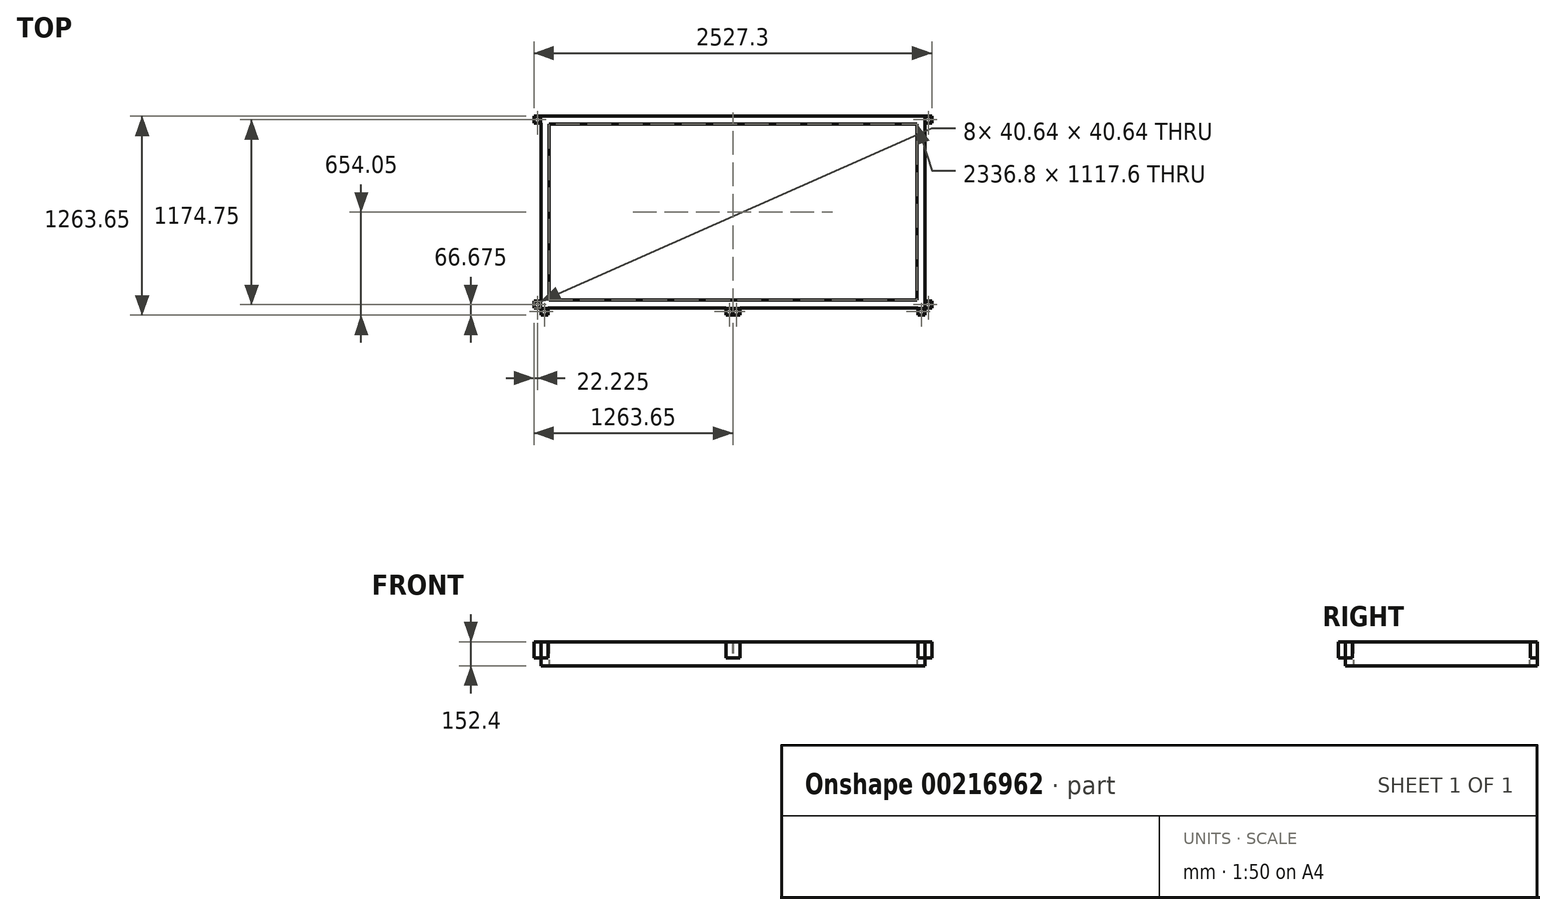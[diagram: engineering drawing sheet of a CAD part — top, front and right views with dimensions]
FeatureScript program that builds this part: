
annotation { "Feature Type Name" : "Feature", "Feature Type Description" : "" }
export const myFeature = defineFeature(function(context is Context, id is Id, definition is map)
    precondition{}
    {
        {
            var Q0;
            Q0=qCreatedBy(makeId("Top.planeOp"),FACE);
            var sketch = newSketch(context, id + "F0", { "sketchPlane" : qUnion([Q0])});
            skLineSegment(sketch, "E0.bottom", {"start": v(1219.2, 609.6) * mm, "end": v(-1219.2, 609.6) * mm});
            skLineSegment(sketch, "E0.top", {"start": v(1219.2, -609.6) * mm, "end": v(-1219.2, -609.6) * mm});
            skLineSegment(sketch, "E0.left", {"start": v(1219.2, 609.6) * mm, "end": v(1219.2, -609.6) * mm});
            skLineSegment(sketch, "E0.right", {"start": v(-1219.2, 609.6) * mm, "end": v(-1219.2, -609.6) * mm});
            skPoint(sketch, "E0.middle", {"position": v(0, 0) * mm});
            skLineSegment(sketch, "E1.bottom", {"start": v(-1219.2, -609.6) * mm, "end": v(-1174.75, -609.6) * mm});
            skLineSegment(sketch, "E1.top", {"start": v(-1219.2, -654.05) * mm, "end": v(-1174.75, -654.05) * mm});
            skLineSegment(sketch, "E1.left", {"start": v(-1219.2, -609.6) * mm, "end": v(-1219.2, -654.05) * mm});
            skLineSegment(sketch, "E1.right", {"start": v(-1174.75, -609.6) * mm, "end": v(-1174.75, -654.05) * mm});
            skLineSegment(sketch, "E2.bottom", {"start": v(-1219.2, -609.6) * mm, "end": v(-1263.65, -609.6) * mm});
            skLineSegment(sketch, "E2.top", {"start": v(-1219.2, -565.15) * mm, "end": v(-1263.65, -565.15) * mm});
            skLineSegment(sketch, "E2.left", {"start": v(-1219.2, -609.6) * mm, "end": v(-1219.2, -565.15) * mm});
            skLineSegment(sketch, "E2.right", {"start": v(-1263.65, -609.6) * mm, "end": v(-1263.65, -565.15) * mm});
            skLineSegment(sketch, "E3.bottom", {"start": v(1219.2, -609.6) * mm, "end": v(1174.75, -609.6) * mm});
            skLineSegment(sketch, "E3.top", {"start": v(1219.2, -654.05) * mm, "end": v(1174.75, -654.05) * mm});
            skLineSegment(sketch, "E3.left", {"start": v(1219.2, -609.6) * mm, "end": v(1219.2, -654.05) * mm});
            skLineSegment(sketch, "E3.right", {"start": v(1174.75, -609.6) * mm, "end": v(1174.75, -654.05) * mm});
            skLineSegment(sketch, "E4.bottom", {"start": v(1219.2, -609.6) * mm, "end": v(1263.65, -609.6) * mm});
            skLineSegment(sketch, "E4.top", {"start": v(1219.2, -565.15) * mm, "end": v(1263.65, -565.15) * mm});
            skLineSegment(sketch, "E4.left", {"start": v(1219.2, -609.6) * mm, "end": v(1219.2, -565.15) * mm});
            skLineSegment(sketch, "E4.right", {"start": v(1263.65, -609.6) * mm, "end": v(1263.65, -565.15) * mm});
            skLineSegment(sketch, "E5.bottom", {"start": v(-1219.2, 609.6) * mm, "end": v(-1263.65, 609.6) * mm});
            skLineSegment(sketch, "E5.top", {"start": v(-1219.2, 565.15) * mm, "end": v(-1263.65, 565.15) * mm});
            skLineSegment(sketch, "E5.left", {"start": v(-1219.2, 609.6) * mm, "end": v(-1219.2, 565.15) * mm});
            skLineSegment(sketch, "E5.right", {"start": v(-1263.65, 609.6) * mm, "end": v(-1263.65, 565.15) * mm});
            skLineSegment(sketch, "E6.bottom", {"start": v(1219.2, 609.6) * mm, "end": v(1263.65, 609.6) * mm});
            skLineSegment(sketch, "E6.top", {"start": v(1219.2, 565.15) * mm, "end": v(1263.65, 565.15) * mm});
            skLineSegment(sketch, "E6.left", {"start": v(1219.2, 609.6) * mm, "end": v(1219.2, 565.15) * mm});
            skLineSegment(sketch, "E6.right", {"start": v(1263.65, 609.6) * mm, "end": v(1263.65, 565.15) * mm});
            skLineSegment(sketch, "E7.bottom", {"start": v(0, -609.6) * mm, "end": v(44.45, -609.6) * mm});
            skLineSegment(sketch, "E7.top", {"start": v(0, -654.05) * mm, "end": v(44.45, -654.05) * mm});
            skLineSegment(sketch, "E7.left", {"start": v(0, -609.6) * mm, "end": v(0, -654.05) * mm});
            skLineSegment(sketch, "E7.right", {"start": v(44.45, -609.6) * mm, "end": v(44.45, -654.05) * mm});
            skLineSegment(sketch, "E8.bottom", {"start": v(0, -609.6) * mm, "end": v(-44.45, -609.6) * mm});
            skLineSegment(sketch, "E8.top", {"start": v(0, -654.05) * mm, "end": v(-44.45, -654.05) * mm});
            skLineSegment(sketch, "E8.right", {"start": v(-44.45, -609.6) * mm, "end": v(-44.45, -654.05) * mm});
            skLineSegment(sketch, "E9.bottom", {"start": v(-1176.65, -611.5) * mm, "end": v(-1217.3, -611.5) * mm});
            skLineSegment(sketch, "E9.top", {"start": v(-1176.65, -652.15) * mm, "end": v(-1217.3, -652.15) * mm});
            skLineSegment(sketch, "E9.left", {"start": v(-1176.65, -611.5) * mm, "end": v(-1176.65, -652.15) * mm});
            skLineSegment(sketch, "E9.right", {"start": v(-1217.3, -611.5) * mm, "end": v(-1217.3, -652.15) * mm});
            skPoint(sketch, "E9.middle", {"position": v(-1196.98, -631.83) * mm});
            skPoint(sketch, "E9.middle.positionSnap0", {"position": v(-1196.98, -609.6) * mm});
            skPoint(sketch, "E9.middle.positionSnap1", {"position": v(-1219.2, -631.83) * mm});
            skPoint(sketch, "E9.centerSnap0", {"position": v(-1196.98, -609.6) * mm});
            skPoint(sketch, "E9.centerSnap1", {"position": v(-1219.2, -631.83) * mm});
            skLineSegment(sketch, "E10.bottom", {"start": v(-1221.1, -567.06) * mm, "end": v(-1261.74, -567.06) * mm});
            skLineSegment(sketch, "E10.top", {"start": v(-1221.1, -607.7) * mm, "end": v(-1261.74, -607.7) * mm});
            skLineSegment(sketch, "E10.left", {"start": v(-1221.1, -567.06) * mm, "end": v(-1221.1, -607.7) * mm});
            skLineSegment(sketch, "E10.right", {"start": v(-1261.74, -567.06) * mm, "end": v(-1261.74, -607.7) * mm});
            skPoint(sketch, "E10.middle", {"position": v(-1241.42, -587.38) * mm});
            skPoint(sketch, "E10.middle.positionSnap0", {"position": v(-1241.42, -565.15) * mm});
            skPoint(sketch, "E10.middle.positionSnap1", {"position": v(-1263.65, -587.38) * mm});
            skPoint(sketch, "E10.centerSnap0", {"position": v(-1241.42, -565.15) * mm});
            skPoint(sketch, "E10.centerSnap1", {"position": v(-1263.65, -587.38) * mm});
            skLineSegment(sketch, "E11.bottom", {"start": v(-1221.1, 607.7) * mm, "end": v(-1261.75, 607.7) * mm});
            skLineSegment(sketch, "E11.top", {"start": v(-1221.1, 567.05) * mm, "end": v(-1261.75, 567.05) * mm});
            skLineSegment(sketch, "E11.left", {"start": v(-1221.1, 607.7) * mm, "end": v(-1221.1, 567.05) * mm});
            skLineSegment(sketch, "E11.right", {"start": v(-1261.75, 607.7) * mm, "end": v(-1261.75, 567.05) * mm});
            skPoint(sketch, "E11.middle", {"position": v(-1241.43, 587.37) * mm});
            skPoint(sketch, "E11.middle.positionSnap0", {"position": v(-1241.43, 609.6) * mm});
            skPoint(sketch, "E11.middle.positionSnap1", {"position": v(-1263.65, 587.37) * mm});
            skPoint(sketch, "E11.centerSnap0", {"position": v(-1241.43, 609.6) * mm});
            skPoint(sketch, "E11.centerSnap1", {"position": v(-1263.65, 587.37) * mm});
            skLineSegment(sketch, "E12.bottom", {"start": v(1261.74, 607.7) * mm, "end": v(1221.1, 607.7) * mm});
            skLineSegment(sketch, "E12.top", {"start": v(1261.75, 567.05) * mm, "end": v(1221.1, 567.06) * mm});
            skLineSegment(sketch, "E12.left", {"start": v(1261.75, 607.7) * mm, "end": v(1261.75, 567.05) * mm});
            skLineSegment(sketch, "E12.right", {"start": v(1221.1, 607.7) * mm, "end": v(1221.1, 567.06) * mm});
            skPoint(sketch, "E12.middle", {"position": v(1241.42, 587.38) * mm});
            skPoint(sketch, "E12.middle.positionSnap0", {"position": v(1263.65, 587.38) * mm});
            skPoint(sketch, "E12.middle.positionSnap1", {"position": v(1241.42, 565.15) * mm});
            skPoint(sketch, "E12.centerSnap0", {"position": v(1263.65, 587.38) * mm});
            skPoint(sketch, "E12.centerSnap1", {"position": v(1241.42, 565.15) * mm});
            skLineSegment(sketch, "E13.bottom", {"start": v(1261.75, -567.05) * mm, "end": v(1221.1, -567.05) * mm});
            skLineSegment(sketch, "E13.top", {"start": v(1261.75, -607.7) * mm, "end": v(1221.1, -607.7) * mm});
            skLineSegment(sketch, "E13.left", {"start": v(1261.75, -567.05) * mm, "end": v(1261.75, -607.7) * mm});
            skLineSegment(sketch, "E13.right", {"start": v(1221.1, -567.05) * mm, "end": v(1221.1, -607.7) * mm});
            skPoint(sketch, "E13.middle", {"position": v(1241.42, -587.38) * mm});
            skPoint(sketch, "E13.middle.positionSnap0", {"position": v(1263.65, -587.38) * mm});
            skPoint(sketch, "E13.middle.positionSnap1", {"position": v(1241.42, -609.6) * mm});
            skPoint(sketch, "E13.centerSnap0", {"position": v(1263.65, -587.38) * mm});
            skPoint(sketch, "E13.centerSnap1", {"position": v(1241.42, -609.6) * mm});
            skLineSegment(sketch, "E14.bottom", {"start": v(1217.3, -611.5) * mm, "end": v(1176.66, -611.5) * mm});
            skLineSegment(sketch, "E14.top", {"start": v(1217.3, -652.14) * mm, "end": v(1176.66, -652.14) * mm});
            skLineSegment(sketch, "E14.left", {"start": v(1217.3, -611.5) * mm, "end": v(1217.3, -652.14) * mm});
            skLineSegment(sketch, "E14.right", {"start": v(1176.66, -611.5) * mm, "end": v(1176.66, -652.14) * mm});
            skPoint(sketch, "E14.middle", {"position": v(1196.98, -631.82) * mm});
            skPoint(sketch, "E14.middle.positionSnap0", {"position": v(1196.98, -654.05) * mm});
            skPoint(sketch, "E14.middle.positionSnap1", {"position": v(1219.2, -631.82) * mm});
            skPoint(sketch, "E14.centerSnap0", {"position": v(1196.98, -654.05) * mm});
            skPoint(sketch, "E14.centerSnap1", {"position": v(1219.2, -631.82) * mm});
            skLineSegment(sketch, "E15.bottom", {"start": v(42.55, -611.5) * mm, "end": v(1.9, -611.5) * mm});
            skLineSegment(sketch, "E15.top", {"start": v(42.55, -652.15) * mm, "end": v(1.9, -652.15) * mm});
            skLineSegment(sketch, "E15.left", {"start": v(42.55, -611.5) * mm, "end": v(42.55, -652.15) * mm});
            skLineSegment(sketch, "E15.right", {"start": v(1.9, -611.5) * mm, "end": v(1.9, -652.15) * mm});
            skPoint(sketch, "E15.middle", {"position": v(22.23, -631.83) * mm});
            skPoint(sketch, "E15.middle.positionSnap0", {"position": v(22.23, -654.05) * mm});
            skPoint(sketch, "E15.middle.positionSnap1", {"position": v(44.45, -631.83) * mm});
            skPoint(sketch, "E15.centerSnap0", {"position": v(22.23, -654.05) * mm});
            skPoint(sketch, "E15.centerSnap1", {"position": v(44.45, -631.83) * mm});
            skLineSegment(sketch, "E16.bottom", {"start": v(-1.9, -611.5) * mm, "end": v(-42.54, -611.5) * mm});
            skLineSegment(sketch, "E16.top", {"start": v(-1.9, -652.15) * mm, "end": v(-42.54, -652.15) * mm});
            skLineSegment(sketch, "E16.left", {"start": v(-1.9, -611.5) * mm, "end": v(-1.9, -652.15) * mm});
            skLineSegment(sketch, "E16.right", {"start": v(-42.54, -611.5) * mm, "end": v(-42.54, -652.15) * mm});
            skPoint(sketch, "E16.middle", {"position": v(-22.22, -631.83) * mm});
            skPoint(sketch, "E16.middle.positionSnap0", {"position": v(-22.22, -654.05) * mm});
            skPoint(sketch, "E16.middle.positionSnap1", {"position": v(-44.45, -631.83) * mm});
            skPoint(sketch, "E16.centerSnap0", {"position": v(-22.22, -654.05) * mm});
            skPoint(sketch, "E16.centerSnap1", {"position": v(-44.45, -631.83) * mm});
            skLineSegment(sketch, "E17.bottom", {"start": v(-1168.4, -558.8) * mm, "end": v(1168.4, -558.8) * mm});
            skLineSegment(sketch, "E17.top", {"start": v(-1168.4, 558.8) * mm, "end": v(1168.4, 558.8) * mm});
            skLineSegment(sketch, "E17.left", {"start": v(-1168.4, -558.8) * mm, "end": v(-1168.4, 558.8) * mm});
            skLineSegment(sketch, "E17.right", {"start": v(1168.4, -558.8) * mm, "end": v(1168.4, 558.8) * mm});
            skSolve(sketch);
        }
        {
            var Q0;
            Q0 = qSketchRegion(id + "F0", true);
            extrude(context, id + "F1", {"entities" : qUnion([Q0]), "depth" : 101.6 * mm, "offsetDistance" : 25.4 * mm});
        }
        {
            var Q0;
            Q0=makeQuery(id+"F1.opExtrude","CAP_FACE",FACE,{"disambiguationData":[OSD([sQuery(id+"F0.wireOp",EDGE,"E0.bottom"),sQuery(id+"F0.wireOp",EDGE,"E0.top"),sQuery(id+"F0.wireOp",EDGE,"E0.left"),sQuery(id+"F0.wireOp",EDGE,"E0.right"),sQuery(id+"F0.wireOp",EDGE,"E1.top"),sQuery(id+"F0.wireOp",EDGE,"E1.left"),sQuery(id+"F0.wireOp",EDGE,"E1.right"),sQuery(id+"F0.wireOp",EDGE,"E2.bottom"),sQuery(id+"F0.wireOp",EDGE,"E2.top"),sQuery(id+"F0.wireOp",EDGE,"E2.right"),sQuery(id+"F0.wireOp",EDGE,"E3.top"),sQuery(id+"F0.wireOp",EDGE,"E3.left"),sQuery(id+"F0.wireOp",EDGE,"E3.right"),sQuery(id+"F0.wireOp",EDGE,"E4.bottom"),sQuery(id+"F0.wireOp",EDGE,"E4.top"),sQuery(id+"F0.wireOp",EDGE,"E4.right"),sQuery(id+"F0.wireOp",EDGE,"E5.bottom"),sQuery(id+"F0.wireOp",EDGE,"E5.top"),sQuery(id+"F0.wireOp",EDGE,"E5.right"),sQuery(id+"F0.wireOp",EDGE,"E6.bottom"),sQuery(id+"F0.wireOp",EDGE,"E6.top"),sQuery(id+"F0.wireOp",EDGE,"E6.right"),sQuery(id+"F0.wireOp",EDGE,"E7.top"),sQuery(id+"F0.wireOp",EDGE,"E7.right"),sQuery(id+"F0.wireOp",EDGE,"E8.top"),sQuery(id+"F0.wireOp",EDGE,"E8.right"),sQuery(id+"F0.wireOp",EDGE,"E9.bottom"),sQuery(id+"F0.wireOp",EDGE,"E9.top"),sQuery(id+"F0.wireOp",EDGE,"E9.left"),sQuery(id+"F0.wireOp",EDGE,"E9.right"),sQuery(id+"F0.wireOp",EDGE,"E10.bottom"),sQuery(id+"F0.wireOp",EDGE,"E10.top"),sQuery(id+"F0.wireOp",EDGE,"E10.left"),sQuery(id+"F0.wireOp",EDGE,"E10.right"),sQuery(id+"F0.wireOp",EDGE,"E11.bottom"),sQuery(id+"F0.wireOp",EDGE,"E11.top"),sQuery(id+"F0.wireOp",EDGE,"E11.left"),sQuery(id+"F0.wireOp",EDGE,"E11.right"),sQuery(id+"F0.wireOp",EDGE,"E12.bottom"),sQuery(id+"F0.wireOp",EDGE,"E12.top"),sQuery(id+"F0.wireOp",EDGE,"E12.left"),sQuery(id+"F0.wireOp",EDGE,"E12.right"),sQuery(id+"F0.wireOp",EDGE,"E13.bottom"),sQuery(id+"F0.wireOp",EDGE,"E13.top"),sQuery(id+"F0.wireOp",EDGE,"E13.left"),sQuery(id+"F0.wireOp",EDGE,"E13.right"),sQuery(id+"F0.wireOp",EDGE,"E14.bottom"),sQuery(id+"F0.wireOp",EDGE,"E14.top"),sQuery(id+"F0.wireOp",EDGE,"E14.left"),sQuery(id+"F0.wireOp",EDGE,"E14.right"),sQuery(id+"F0.wireOp",EDGE,"E15.bottom"),sQuery(id+"F0.wireOp",EDGE,"E15.top"),sQuery(id+"F0.wireOp",EDGE,"E15.left"),sQuery(id+"F0.wireOp",EDGE,"E15.right"),sQuery(id+"F0.wireOp",EDGE,"E16.bottom"),sQuery(id+"F0.wireOp",EDGE,"E16.top"),sQuery(id+"F0.wireOp",EDGE,"E16.left"),sQuery(id+"F0.wireOp",EDGE,"E16.right"),sQuery(id+"F0.wireOp",EDGE,"E17.bottom"),sQuery(id+"F0.wireOp",EDGE,"E17.top"),sQuery(id+"F0.wireOp",EDGE,"E17.left"),sQuery(id+"F0.wireOp",EDGE,"E17.right")])],"isStart":true});
            var sketch = newSketch(context, id + "F2", { "sketchPlane" : qUnion([Q0])});
            skLineSegment(sketch, "E18.bottom", {"start": v(-1219.2, 609.6) * mm, "end": v(1219.2, 609.6) * mm});
            skLineSegment(sketch, "E18.top", {"start": v(-1219.2, -609.6) * mm, "end": v(1219.2, -609.6) * mm});
            skLineSegment(sketch, "E18.left", {"start": v(-1219.2, 609.6) * mm, "end": v(-1219.2, -609.6) * mm});
            skLineSegment(sketch, "E18.right", {"start": v(1219.2, 609.6) * mm, "end": v(1219.2, -609.6) * mm});
            skPoint(sketch, "E18.middle", {"position": v(0, 0) * mm});
            skLineSegment(sketch, "E19.bottom", {"start": v(1168.4, 558.8) * mm, "end": v(-1168.4, 558.8) * mm});
            skLineSegment(sketch, "E19.top", {"start": v(1168.4, -558.8) * mm, "end": v(-1168.4, -558.8) * mm});
            skLineSegment(sketch, "E19.left", {"start": v(1168.4, 558.8) * mm, "end": v(1168.4, -558.8) * mm});
            skLineSegment(sketch, "E19.right", {"start": v(-1168.4, 558.8) * mm, "end": v(-1168.4, -558.8) * mm});
            skSolve(sketch);
        }
        {
            var Q0;
            Q0 = qSketchRegion(id + "F2", true);
            extrude(context, id + "F3", {"entities" : qUnion([Q0]), "operationType" : NewBodyOperationType.ADD, "depth" : 50.8 * mm, "offsetDistance" : 25.4 * mm});
        }
    });
